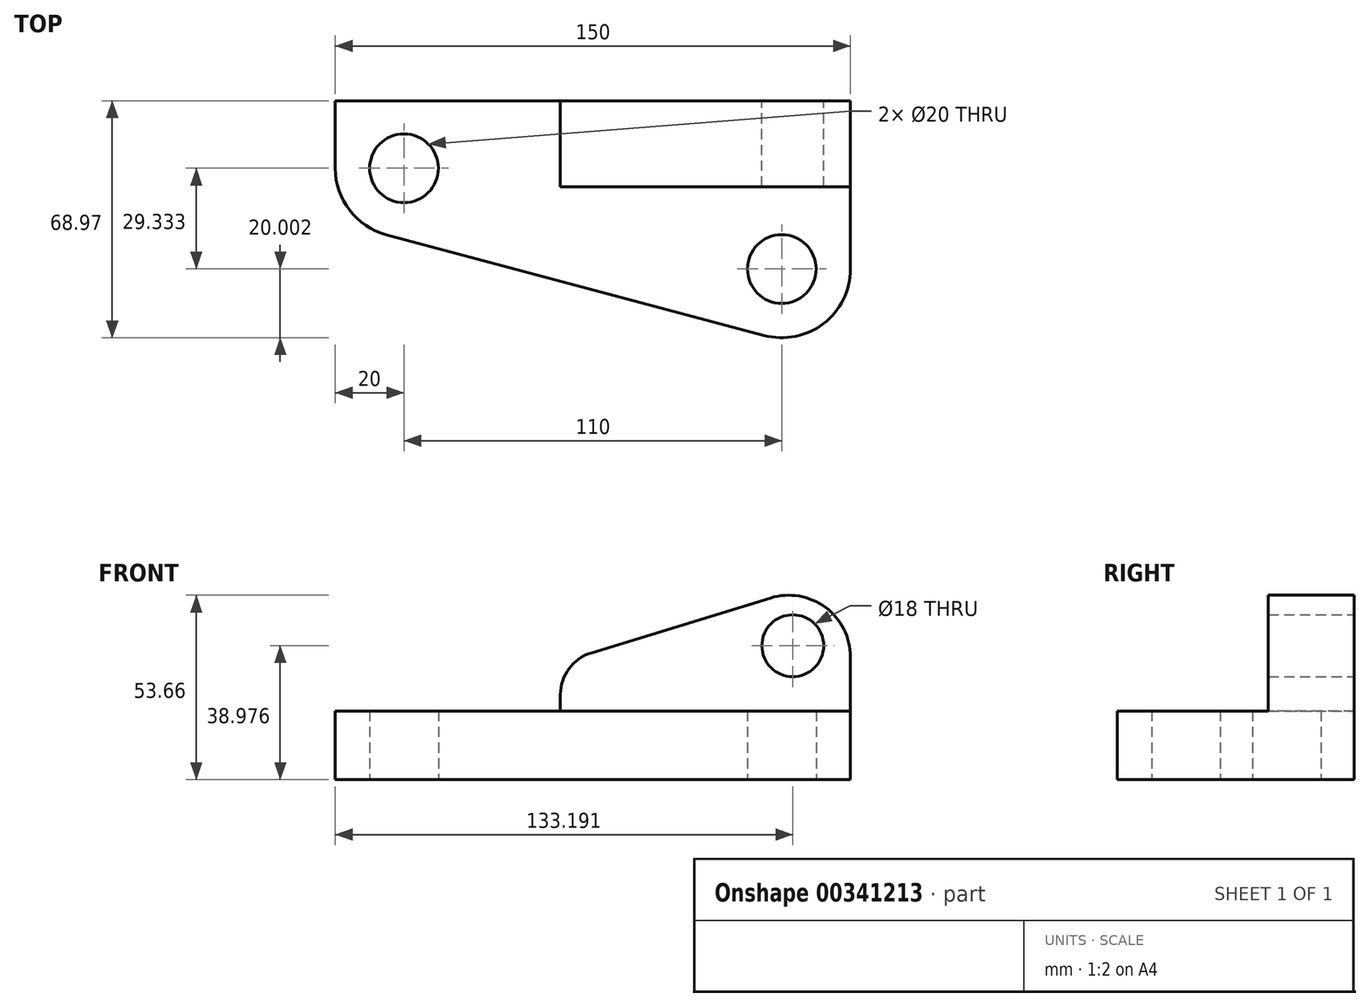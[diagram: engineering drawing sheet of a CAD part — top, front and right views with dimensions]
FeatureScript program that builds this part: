
annotation { "Feature Type Name" : "Feature", "Feature Type Description" : "" }
export const myFeature = defineFeature(function(context is Context, id is Id, definition is map)
    precondition{}
    {
        {
            var Q0;
            Q0=qCreatedBy(makeId("Top.planeOp"),FACE);
            var sketch = newSketch(context, id + "F0", { "sketchPlane" : qUnion([Q0])});
            skLineSegment(sketch, "E0", {"start": v(0, 0) * mm, "end": v(0, -48.97) * mm});
            skLineSegment(sketch, "E1", {"start": v(0, 0) * mm, "end": v(-150, 0) * mm});
            skLineSegment(sketch, "E2", {"start": v(-150, 0) * mm, "end": v(-150, -19.63) * mm});
            skLineSegment(sketch, "E3", {"start": v(-135.15, -38.96) * mm, "end": v(-25.15, -68.3) * mm});
            skPoint(sketch, "E4.visualSharp", {"position": v(-150, -35) * mm});
            skArc(sketch, "E4.filletArc", {"start": v(-150, -19.63) * mm, "mid": v(-145.86, -31.82) * mm, "end": v(-135.15, -38.96) * mm});
            skPoint(sketch, "E5.visualSharp", {"position": v(0, -75) * mm});
            skArc(sketch, "E5.filletArc", {"start": v(-25.15, -68.3) * mm, "mid": v(-7.82, -64.83) * mm, "end": v(0, -48.97) * mm});
            skCircle(sketch, "E6", {"center": v(-20, -48.97) * mm, "radius": 10 * mm});
            skCircle(sketch, "E7", {"center": v(-130, -19.63) * mm, "radius": 10 * mm});
            skSolve(sketch);
        }
        {
            var Q0;
            Q0 = qSketchRegion(id + "F0", true);
            extrude(context, id + "F1", {"entities" : qUnion([Q0]), "depth" : 20 * mm});
        }
        {
            var Q0;
            Q0=qCreatedBy(makeId("Front.planeOp"),FACE);
            var sketch = newSketch(context, id + "F2", { "sketchPlane" : qUnion([Q0])});
            skLineSegment(sketch, "E8", {"start": v(0, 0) * mm, "end": v(0, 35.66) * mm});
            skLineSegment(sketch, "E9", {"start": v(-23.27, 52.87) * mm, "end": v(-75.47, 36.89) * mm});
            skLineSegment(sketch, "E10", {"start": v(-84.45, 0) * mm, "end": v(0, 0) * mm});
            skLineSegment(sketch, "E11", {"start": v(-84.45, 24.75) * mm, "end": v(-84.45, 0) * mm});
            skPoint(sketch, "E12.visualSharp", {"position": v(0, 60) * mm});
            skArc(sketch, "E12.filletArc", {"start": v(0, 35.66) * mm, "mid": v(-7.3, 50.13) * mm, "end": v(-23.27, 52.87) * mm});
            skPoint(sketch, "E13.visualSharp", {"position": v(-84.45, 34.14) * mm});
            skArc(sketch, "E13.filletArc", {"start": v(-75.47, 36.89) * mm, "mid": v(-81.96, 32.3) * mm, "end": v(-84.45, 24.75) * mm});
            skCircle(sketch, "E14", {"center": v(-16.8, 38.98) * mm, "radius": 9 * mm});
            skSolve(sketch);
        }
        {
            var Q0;
            Q0 = qSketchRegion(id + "F2", true);
            extrude(context, id + "F3", {"entities" : qUnion([Q0]), "operationType" : NewBodyOperationType.ADD, "depth" : 25 * mm});
        }
    });
